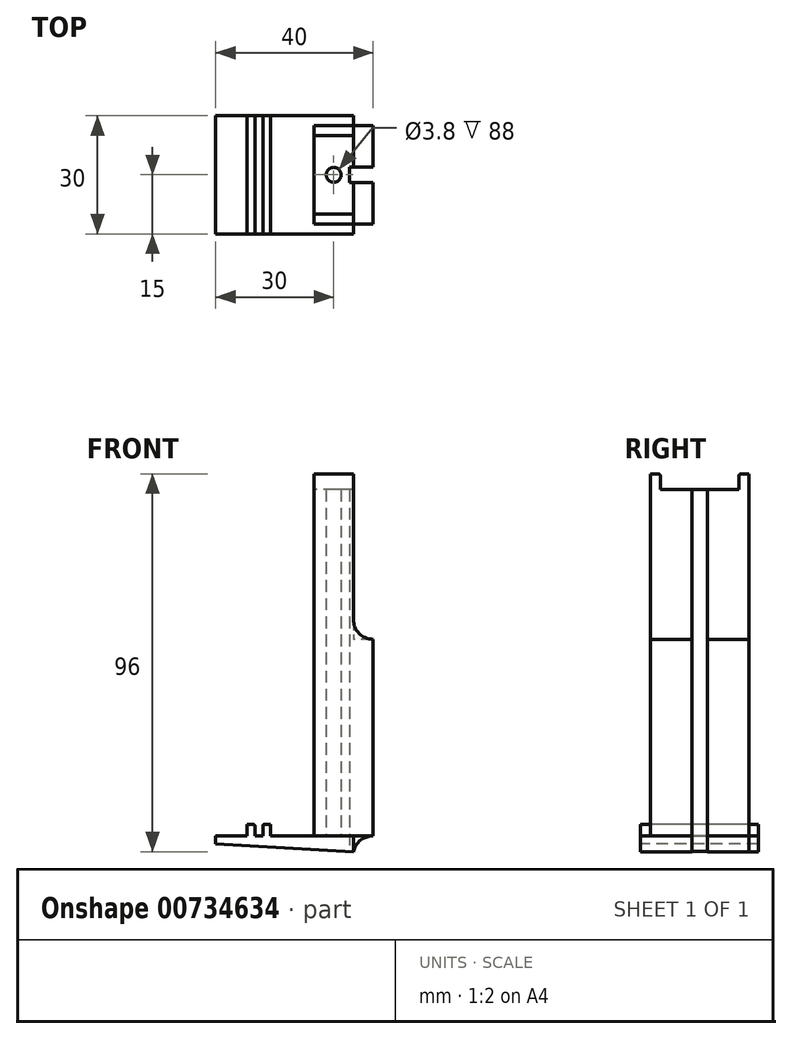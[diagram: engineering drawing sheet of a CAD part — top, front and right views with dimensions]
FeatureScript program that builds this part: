
annotation { "Feature Type Name" : "Feature", "Feature Type Description" : "" }
export const myFeature = defineFeature(function(context is Context, id is Id, definition is map)
    precondition{}
    {
        {
            var Q0;
            Q0=qCreatedBy(makeId("Top.planeOp"),FACE);
            var sketch = newSketch(context, id + "F0", { "sketchPlane" : qUnion([Q0])});
            skLineSegment(sketch, "E0.bottom", {"start": v(0, 15) * mm, "end": v(-35, 15) * mm});
            skLineSegment(sketch, "E0.top", {"start": v(0, -15) * mm, "end": v(-35, -15) * mm});
            skLineSegment(sketch, "E0.left", {"start": v(0, 15) * mm, "end": v(0, 2) * mm});
            skLineSegment(sketch, "E0.right", {"start": v(-35, 15) * mm, "end": v(-35, -15) * mm});
            skPoint(sketch, "E1.visualSharp", {"position": v(-35, 15) * mm});
            skLineSegment(sketch, "E1.filletArc", {"start": v(-35, 15) * mm, "end": v(-35, 15) * mm});
            skPoint(sketch, "E2.visualSharp", {"position": v(-35, -15) * mm});
            skLineSegment(sketch, "E2.filletArc", {"start": v(-35, -15) * mm, "end": v(-35, -15) * mm});
            skPoint(sketch, "E3.visualSharp", {"position": v(0, -15) * mm});
            skLineSegment(sketch, "E3.filletArc", {"start": v(0, -15) * mm, "end": v(0, -15) * mm});
            skPoint(sketch, "E4.visualSharp", {"position": v(0, 15) * mm});
            skLineSegment(sketch, "E4.filletArc", {"start": v(0, 15) * mm, "end": v(0, 15) * mm});
            skLineSegment(sketch, "E5.bottom", {"start": v(0, 2) * mm, "end": v(-1, 2) * mm});
            skLineSegment(sketch, "E5.top", {"start": v(0, -2) * mm, "end": v(-1, -2) * mm});
            skLineSegment(sketch, "E5.right", {"start": v(-1, 2) * mm, "end": v(-1, -2) * mm});
            skLineSegment(sketch, "E6.trimOffspring", {"start": v(0, -2) * mm, "end": v(0, -15) * mm});
            skSolve(sketch);
        }
        {
            var Q0;
            Q0 = qSketchRegion(id + "F0", true);
            extrude(context, id + "F1", {"entities" : qUnion([Q0]), "depth" : 2 * mm, "offsetDistance" : 25 * mm});
        }
        {
            var Q0;
            Q0=makeQuery(id+"F1.opExtrude","CAP_FACE",FACE,{"disambiguationData":[OSD([sQuery(id+"F0.wireOp",EDGE,"E0.bottom"),sQuery(id+"F0.wireOp",EDGE,"E0.top"),sQuery(id+"F0.wireOp",EDGE,"E0.left"),sQuery(id+"F0.wireOp",EDGE,"E0.right"),sQuery(id+"F0.wireOp",EDGE,"E1.filletArc"),sQuery(id+"F0.wireOp",EDGE,"E2.filletArc"),sQuery(id+"F0.wireOp",EDGE,"E3.filletArc"),sQuery(id+"F0.wireOp",EDGE,"E4.filletArc")])],"isStart":false});
            var sketch = newSketch(context, id + "F2", { "sketchPlane" : qUnion([Q0])});
            skLineSegment(sketch, "E7.bottom", {"start": v(0, 2) * mm, "end": v(-1, 2) * mm});
            skLineSegment(sketch, "E7.top", {"start": v(0, -2) * mm, "end": v(-1, -2) * mm});
            skLineSegment(sketch, "E7.right", {"start": v(-1, 2) * mm, "end": v(-1, -2) * mm});
            skCircle(sketch, "E8", {"center": v(-5, 0) * mm, "radius": 1.9 * mm});
            skLineSegment(sketch, "E9.bottom", {"start": v(0, 10) * mm, "end": v(-10, 10) * mm});
            skLineSegment(sketch, "E9.top", {"start": v(0, -10) * mm, "end": v(-10, -10) * mm});
            skLineSegment(sketch, "E9.left", {"start": v(0, 10) * mm, "end": v(0, 2) * mm});
            skLineSegment(sketch, "E9.right", {"start": v(-10, 10) * mm, "end": v(-10, -10) * mm});
            skLineSegment(sketch, "E10.trimOffspring", {"start": v(0, -2) * mm, "end": v(0, -10) * mm});
            skSolve(sketch);
        }
        {
            var Q0;
            Q0 = qSketchRegion(id + "F2", true);
            extrude(context, id + "F3", {"entities" : qUnion([Q0]), "operationType" : NewBodyOperationType.ADD, "depth" : 88 * mm, "offsetDistance" : 25 * mm});
        }
        {
            var Q0;
            {var subQ0=sQuery(id+"F0.wireOp",EDGE,"E0.left");var subQ1=sQuery(id+"F0.wireOp",EDGE,"E4.filletArc");var subQ2=sQuery(id+"F0.wireOp",EDGE,"E3.filletArc");var subQ3=sQuery(id+"F0.wireOp",EDGE,"E2.filletArc");var subQ4=sQuery(id+"F0.wireOp",EDGE,"E1.filletArc");var subQ5=sQuery(id+"F0.wireOp",EDGE,"E0.bottom");var subQ6=sQuery(id+"F0.wireOp",EDGE,"E0.right");var subQ7=sQuery(id+"F0.wireOp",EDGE,"E0.top");Q0=makeQuery(id+"F3.boolean.opBoolean","SPLIT",FACE,{"disambiguationData":[TD([makeQuery(id+"F1.opExtrude","SWEPT_FACE",FACE,{"disambiguationData":[OSD([subQ5])]})])],"derivedFrom":makeQuery(id+"F1.opExtrude","CAP_FACE",FACE,{"disambiguationData":[OSD([subQ5,subQ7,subQ0,subQ6,subQ4,subQ3,subQ2,subQ1])],"isStart":false})});}
            var sketch = newSketch(context, id + "F4", { "sketchPlane" : qUnion([Q0])});
            skLineSegment(sketch, "E11", {"start": v(-25, 15) * mm, "end": v(-25, -15) * mm, "construction": true});
            skLineSegment(sketch, "E12.bottom", {"start": v(-25, 15) * mm, "end": v(-27, 15) * mm});
            skLineSegment(sketch, "E12.top", {"start": v(-25, -15) * mm, "end": v(-27, -15) * mm});
            skLineSegment(sketch, "E12.left", {"start": v(-25, 15) * mm, "end": v(-25, -15) * mm});
            skLineSegment(sketch, "E12.right", {"start": v(-27, 15) * mm, "end": v(-27, -15) * mm});
            skLineSegment(sketch, "E13.bottom", {"start": v(-23, 15) * mm, "end": v(-21, 15) * mm});
            skLineSegment(sketch, "E13.top", {"start": v(-23, -15) * mm, "end": v(-21, -15) * mm});
            skLineSegment(sketch, "E13.left", {"start": v(-23, 15) * mm, "end": v(-23, -15) * mm});
            skLineSegment(sketch, "E13.right", {"start": v(-21, 15) * mm, "end": v(-21, -15) * mm});
            skSolve(sketch);
        }
        {
            var Q0;
            Q0 = qSketchRegion(id + "F4", true);
            extrude(context, id + "F5", {"entities" : qUnion([Q0]), "operationType" : NewBodyOperationType.ADD, "depth" : 3 * mm, "offsetDistance" : 25 * mm});
        }
        {
            var Q0;
            Q0=makeQuery(id+"F1.opExtrude","CAP_FACE",FACE,{"disambiguationData":[OSD([sQuery(id+"F0.wireOp",EDGE,"E0.bottom"),sQuery(id+"F0.wireOp",EDGE,"E0.top"),sQuery(id+"F0.wireOp",EDGE,"E0.left"),sQuery(id+"F0.wireOp",EDGE,"E0.right"),sQuery(id+"F0.wireOp",EDGE,"E1.filletArc"),sQuery(id+"F0.wireOp",EDGE,"E2.filletArc"),sQuery(id+"F0.wireOp",EDGE,"E3.filletArc"),sQuery(id+"F0.wireOp",EDGE,"E4.filletArc")])],"isStart":true});
            extrude(context, id + "F6", {"entities" : qUnion([Q0]), "operationType" : NewBodyOperationType.ADD, "depth" : 2 * mm, "offsetDistance" : 25 * mm});
        }
        {
            var Q0;
            {var subQ0=sQuery(id+"F0.wireOp",EDGE,"E0.top");Q0=makeQuery(id+"F6.boolean.opBoolean","MERGE",FACE,{"derivedFrom":[makeQuery(id+"F5.boolean.opBoolean","MERGE",FACE,{"derivedFrom":[makeQuery(id+"F1.opExtrude","SWEPT_FACE",FACE,{"disambiguationData":[OSD([subQ0])]}),makeQuery(id+"F5.opExtrude","SWEPT_FACE",FACE,{"disambiguationData":[OSD([sQuery(id+"F4.wireOp",EDGE,"E12.top")])]}),makeQuery(id+"F5.opExtrude","SWEPT_FACE",FACE,{"disambiguationData":[OSD([sQuery(id+"F4.wireOp",EDGE,"E13.top")])]})]}),makeQuery(id+"F6.opExtrude","SWEPT_FACE",FACE,{"disambiguationData":[OSD([subQ0])]})]});}
            var sketch = newSketch(context, id + "F7", { "sketchPlane" : qUnion([Q0])});
            skLineSegment(sketch, "E14", {"start": v(-35, 0) * mm, "end": v(0, -2) * mm});
            skLineSegment(sketch, "E15", {"start": v(-35, 0) * mm, "end": v(-35, -2) * mm});
            skLineSegment(sketch, "E16", {"start": v(-35, -2) * mm, "end": v(0, -2) * mm});
            skSolve(sketch);
        }
        {
            var Q0;
            Q0 = qSketchRegion(id + "F7", true);
            extrude(context, id + "F8", {"entities" : qUnion([Q0]), "operationType" : NewBodyOperationType.REMOVE, "endBound" : BoundingType.THROUGH_ALL, "oppositeDirection" : true, "depth" : 25 * mm, "offsetDistance" : 25 * mm});
        }
        {
            var Q0;
            {var subQ4=sQuery(id+"F0.wireOp",EDGE,"E0.bottom");var subQ5=makeQuery(id+"F1.opExtrude","SWEPT_FACE",FACE,{"disambiguationData":[OSD([subQ4])]});var subQ6=sQuery(id+"F0.wireOp",EDGE,"E0.top");var subQ8=sQuery(id+"F0.wireOp",EDGE,"E0.left");var subQ9=makeQuery(id+"F1.opExtrude","SWEPT_FACE",FACE,{"disambiguationData":[OSD([subQ8])]});var subQ11=sQuery(id+"F0.wireOp",EDGE,"E6.trimOffspring");var subQ13=sQuery(id+"F0.wireOp",EDGE,"E0.right");Q0=makeQuery(id+"F5.boolean.opBoolean","SPLIT",FACE,{"disambiguationData":[TD([subQ9])],"derivedFrom":makeQuery(id+"F3.boolean.opBoolean","SPLIT",FACE,{"disambiguationData":[TD([subQ5])],"derivedFrom":makeQuery(id+"F1.opExtrude","CAP_FACE",FACE,{"disambiguationData":[OSD([subQ4,subQ6,subQ8,subQ13,sQuery(id+"F0.wireOp",EDGE,"E5.bottom"),sQuery(id+"F0.wireOp",EDGE,"E5.top"),sQuery(id+"F0.wireOp",EDGE,"E5.right"),subQ11])],"isStart":false})})});}
            var sketch = newSketch(context, id + "F9", { "sketchPlane" : qUnion([Q0])});
            skLineSegment(sketch, "E17.bottom", {"start": v(-10, 10) * mm, "end": v(0, 10) * mm});
            skLineSegment(sketch, "E17.top", {"start": v(-10, 12.5) * mm, "end": v(0, 12.5) * mm});
            skLineSegment(sketch, "E17.left", {"start": v(-10, 10) * mm, "end": v(-10, 12.5) * mm});
            skLineSegment(sketch, "E17.right", {"start": v(0, 10) * mm, "end": v(0, 12.5) * mm});
            skLineSegment(sketch, "E18.MirrorCS", {"start": v(-10, -10) * mm, "end": v(-10, -12.5) * mm});
            skLineSegment(sketch, "E19.MirrorCS", {"start": v(-10, -12.5) * mm, "end": v(0, -12.5) * mm});
            skLineSegment(sketch, "E20.MirrorCS", {"start": v(-10, -10) * mm, "end": v(0, -10) * mm});
            skLineSegment(sketch, "E21.MirrorCS", {"start": v(0, -10) * mm, "end": v(0, -12.5) * mm});
            skSolve(sketch);
        }
        {
            var Q0;
            Q0 = qSketchRegion(id + "F9", true);
            extrude(context, id + "F10", {"entities" : qUnion([Q0]), "operationType" : NewBodyOperationType.ADD, "depth" : 92 * mm, "offsetDistance" : 25 * mm});
        }
        {
            var Q0;
            Q0=makeQuery(id+"F5.opExtrude","CAP_EDGE",EDGE,{"disambiguationData":[OSD([sQuery(id+"F4.wireOp",EDGE,"E12.left")])],"isStart":false});
            var Q1;
            Q1=makeQuery(id+"F5.opExtrude","CAP_EDGE",EDGE,{"disambiguationData":[OSD([sQuery(id+"F4.wireOp",EDGE,"E13.left")])],"isStart":false});
            var Q2;
            Q2=makeQuery(id+"F10.opExtrude","CAP_EDGE",EDGE,{"disambiguationData":[OSD([sQuery(id+"F9.wireOp",EDGE,"E17.bottom")])],"isStart":false});
            var Q3;
            Q3=makeQuery(id+"F10.opExtrude","CAP_EDGE",EDGE,{"disambiguationData":[OSD([sQuery(id+"F9.wireOp",EDGE,"E20.MirrorCS")])],"isStart":false});
            fillet(context, id + "F11", {"entities" : qUnion([Q0, Q1, Q2, Q3]), "tangentPropagation" : true, "radius" : 0.5 * mm, "defaultsChanged" : false, "vertexSettings" : [], "allowEdgeOverflow" : false});
        }
        {
            var Q0;
            {var subQ0=sQuery(id+"F0.wireOp",EDGE,"E0.left");Q0=makeQuery(id+"F10.boolean.opBoolean","MERGE",FACE,{"derivedFrom":[makeQuery(id+"F6.boolean.opBoolean","MERGE",FACE,{"derivedFrom":[makeQuery(id+"F3.boolean.opBoolean","MERGE",FACE,{"derivedFrom":[makeQuery(id+"F1.opExtrude","SWEPT_FACE",FACE,{"disambiguationData":[OSD([subQ0])]}),makeQuery(id+"F3.opExtrude","SWEPT_FACE",FACE,{"disambiguationData":[OSD([sQuery(id+"F2.wireOp",EDGE,"E9.left")])]})]}),makeQuery(id+"F6.opExtrude","SWEPT_FACE",FACE,{"disambiguationData":[OSD([subQ0])]})]}),makeQuery(id+"F10.opExtrude","SWEPT_FACE",FACE,{"disambiguationData":[OSD([sQuery(id+"F9.wireOp",EDGE,"E17.right")])]})]});}
            var sketch = newSketch(context, id + "F12", { "sketchPlane" : qUnion([Q0])});
            skLineSegment(sketch, "E22.bottom", {"start": v(12.5, 2) * mm, "end": v(2, 2) * mm});
            skLineSegment(sketch, "E22.top", {"start": v(12.5, 52) * mm, "end": v(2, 52) * mm});
            skLineSegment(sketch, "E22.left", {"start": v(12.5, 2) * mm, "end": v(12.5, 52) * mm});
            skLineSegment(sketch, "E22.right", {"start": v(2, 2) * mm, "end": v(2, 52) * mm});
            skLineSegment(sketch, "E23.MirrorCS", {"start": v(-12.5, 2) * mm, "end": v(-12.5, 52) * mm});
            skLineSegment(sketch, "E24.MirrorCS", {"start": v(-12.5, 52) * mm, "end": v(-2, 52) * mm});
            skLineSegment(sketch, "E25.MirrorCS", {"start": v(-12.5, 2) * mm, "end": v(-2, 2) * mm});
            skLineSegment(sketch, "E26.MirrorCS", {"start": v(-2, 2) * mm, "end": v(-2, 52) * mm});
            skSolve(sketch);
        }
        {
            var Q0;
            Q0 = qSketchRegion(id + "F12", true);
            extrude(context, id + "F13", {"entities" : qUnion([Q0]), "operationType" : NewBodyOperationType.ADD, "depth" : 5 * mm, "offsetDistance" : 25 * mm});
        }
        {
            var Q0;
            Q0=makeQuery(id+"F13.opExtrude","CAP_EDGE",EDGE,{"disambiguationData":[OSD([sQuery(id+"F12.wireOp",EDGE,"E25.MirrorCS")])],"isStart":true});
            var Q1;
            Q1=makeQuery(id+"F13.opExtrude","CAP_EDGE",EDGE,{"disambiguationData":[OSD([sQuery(id+"F12.wireOp",EDGE,"E22.bottom")])],"isStart":true});
            var Q2;
            Q2=makeQuery(id+"F13.opExtrude","CAP_EDGE",EDGE,{"disambiguationData":[OSD([sQuery(id+"F12.wireOp",EDGE,"E24.MirrorCS")])],"isStart":true});
            var Q3;
            Q3=makeQuery(id+"F13.opExtrude","CAP_EDGE",EDGE,{"disambiguationData":[OSD([sQuery(id+"F12.wireOp",EDGE,"E22.top")])],"isStart":true});
            fillet(context, id + "F14", {"entities" : qUnion([Q0, Q1, Q2, Q3]), "tangentPropagation" : true, "radius" : 5 * mm, "defaultsChanged" : false, "vertexSettings" : [], "allowEdgeOverflow" : false});
        }
    });
